# Revit family: Pantalla Modelo P_LPSM16.1
name_source: partatom
category: Luminarias
units: mm (PartAtom-declared; Revit-internal decimal feet)

## family parameters
Compartido = No
Corte con vacíos al cargar = No
Cota de conector redondo = Diámetro de uso
Origen de luz = No
Punto de cálculo de habitación = No
Se basa en plano de trabajo = Sí
Siempre vertical = No
Tipo de pieza = Normal

## types (1)
- Pantalla Modelo P_LPSM16.1
    Comentarios de vataje = 200-240V
    Descripción = PANTALLA CON TIPO DE LED SMD, PIXEL PITCH 16MM, MIDE 320X320MM DE PANEL Y 17MM DE ESPESOR, RESOLUCION DE 20X20 DOT, CONFIRGURACION DE PANEL DE 1R1G1B, PESO DE 395 gr, POTENCIA DE 720W, ALIMENTADA A 200-240V, CORRIENTE DE MODULO 14.4ª, ANGULO DE VISUALIZACION EN 140 GRADOS EN HORIZONTAL Y 120 GRADOS EN EL PLANO VERTICAL, DISTANCIA DE VISUALIZACION A 10M, ESCALA DE GRISES 65536 PASOS, TEMPERATURA A 8086K, FRECUENCIA A 60Hz, VELOCIDAD DE ACTUALIZACION A 65536Hz, TIPO DE SEÑAL COMO VIDEO/VGA/COMPUTER CONTROL, 24 HORAS CONTINUAS DE TRABAJO, 100 MIL HORAS DE VIDA PROMEDIO, CONTROL A DISTANCIA 100M (ETHERNET)//500M(MULTI-FIBER)//1KM(SINGLE FIBER), TEMPERATURA DE OPERACIÓN -10C HASTA +50C, HUMEDAD DE 10% A 98% RH, IP 65. EQUIPO AUXILIAR NO INCLUIDO: CONTROLADOR DE SISTEMA (XLS16V.1).
    Elevación por defecto = 0 mm  [stored 0 ft]
    Espesor = 17 mm
    Fabricante = BRILLANT
    Lámpara = SMD
    Modelo = LPSM16.1
    Modulo = 320 mm
    Watt per fixture = 720

note: [stored X ft] marks values corroborated as IEEE doubles in the binary element streams (Revit-internal decimal feet)

## geometry (parser evidence)
native form markers: Blend x2
no freeform markers — native parametric forms only
